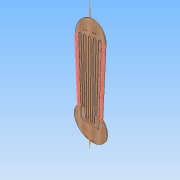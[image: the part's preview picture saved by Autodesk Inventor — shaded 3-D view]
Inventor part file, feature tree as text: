
AUTODESK INVENTOR PART (.ipt)
format: ipt  version: 2013 (Build 170138000, 138)  size: 290,816 bytes
history: native  units: in
note: dims shown in document units (in); Inventor stores cm internally (conversion verified against a paired STEP export)
features: other x5, extrude x3, reference x3, hole x2, sketch x2, plane x1, projected_geometry x1
ambient origin geometry x8: Origin, YZ Plane, XZ Plane, XY Plane, X Axis, Y Axis, Z Axis, Center Point
bodies: Solid1 (feature_tree)
feature tree (17):
  other  "HOT Ply back"
  other  "Blocks"
  extrude  "Extrusion1"  Depth=17.0in
  hole  "Hole Sketch"  [1 undecoded]
  other  "Work Axis1"
  hole  "Hole1"  [1 undecoded]
  extrude  "Extrusion2"  Depth=4.0in
  extrude  "Through Hole"  Depth=1.8125in
  other  "Cut thermo stock"
  plane  "Work Plane1"
  projected_geometry  "Projected Loop1"
  sketch  "Sketch3"  dims[d0=95.5in d2=17.0in]
  other  "One rope curve"
  reference  "Reference1"
  reference  "Reference2"
  reference  "Reference3"
  sketch  "Sketch4"  dims[d3=12.0in d4=0.71in d5=0.0in d8=1.8125in d9=4.0in d10=1.8125in d11=1.8125in d12=0.75in d13=0.75in d14=2.0in d15=15.625in d16=6.302in d17=86.0in d18=0.375in d19=0.75in d20=0.75in d21=0.25in d42=0.5635in d23=1.0in d24=0.8108in d31=52.0in d32=1.24in d33=1.24in d34=0.48in d37=2.5in d39=1.0in d40=1.0in d41=2.0in d43=52.0in d44=1.24in d45=1.24in d46=0.48in d47=52.0in d48=0.48in d49=1.0in d50=62.0in d51=1.24in d52=1.24in d53=0.48in d54=52.0in d55=0.48in d56=1.0in d57=62.0in d58=1.24in d59=1.24in d61=52.0in d62=0.48in d63=1.0in d64=52.0in d65=1.24in d66=1.24in d67=0.48in d68=52.0in d69=0.48in d70=1.0in d71=1.0in d72=0.5in d73=0.0in d74=2.0in d75=2.0in d76=1.0in d77=2.5in d78=1.0in d79=2.25in d80=1.75in d81=0.1875in d82=0.0in d83=0.0in d84=0.0625in]
note: 2 required parameter values undecoded (feature->parameter linkage not recoverable at this tier; creation-order binding heuristic only, values carry confidence <= 0.55)
